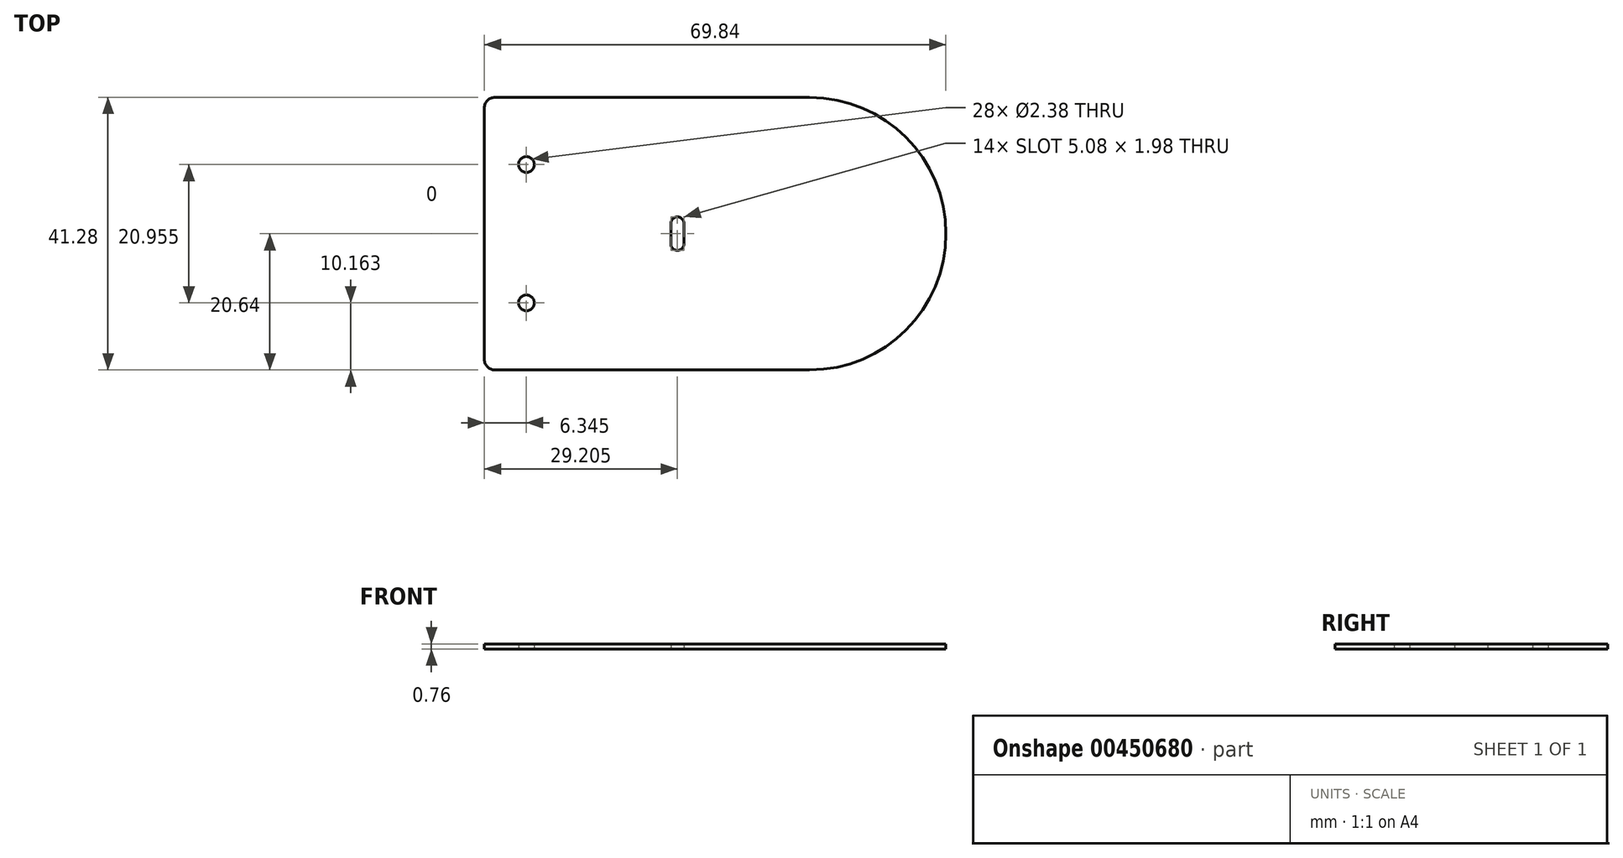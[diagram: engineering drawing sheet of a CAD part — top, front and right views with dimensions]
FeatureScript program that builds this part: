
annotation { "Feature Type Name" : "Feature", "Feature Type Description" : "" }
export const myFeature = defineFeature(function(context is Context, id is Id, definition is map)
    precondition{}
    {
        {
            var Q0;
            Q0=qCreatedBy(makeId("Top.planeOp"),FACE);
            var sketch = newSketch(context, id + "F0", { "sketchPlane" : qUnion([Q0])});
            skLineSegment(sketch, "E0.bottom", {"start": v(14.29, -20.64) * mm, "end": v(-33.34, -20.64) * mm});
            skLineSegment(sketch, "E0.top", {"start": v(14.29, 20.64) * mm, "end": v(-33.34, 20.64) * mm});
            skLineSegment(sketch, "E0.left", {"start": v(34.93, 0) * mm, "end": v(34.93, 0) * mm});
            skLineSegment(sketch, "E0.right", {"start": v(-34.93, -19.05) * mm, "end": v(-34.93, 19.05) * mm});
            skPoint(sketch, "E0.middle", {"position": v(0, 0) * mm});
            skPoint(sketch, "E1.visualSharp", {"position": v(34.93, 20.64) * mm});
            skArc(sketch, "E1.filletArc", {"start": v(34.93, 0) * mm, "mid": v(28.88, 14.6) * mm, "end": v(14.29, 20.64) * mm});
            skPoint(sketch, "E2.visualSharp", {"position": v(34.92, -20.64) * mm});
            skArc(sketch, "E2.filletArc", {"start": v(14.29, -20.64) * mm, "mid": v(28.88, -14.6) * mm, "end": v(34.92, 0) * mm});
            skPoint(sketch, "E3", {"position": v(-34.93, 0) * mm});
            skLineSegment(sketch, "E4.left", {"start": v(-4.72, -1.55) * mm, "end": v(-4.72, 1.55) * mm});
            skLineSegment(sketch, "E4.right", {"start": v(-6.7, -1.55) * mm, "end": v(-6.7, 1.55) * mm});
            skPoint(sketch, "E4.middle", {"position": v(-5.72, 0) * mm});
            skArc(sketch, "E5", {"start": v(-6.7, 1.55) * mm, "mid": v(-5.72, 2.54) * mm, "end": v(-4.72, 1.55) * mm});
            skArc(sketch, "E6", {"start": v(-6.7, -1.55) * mm, "mid": v(-5.72, -2.54) * mm, "end": v(-4.72, -1.55) * mm});
            skPoint(sketch, "E7", {"position": v(-5.72, 2.54) * mm});
            skPoint(sketch, "E8", {"position": v(-5.72, -2.54) * mm});
            skPoint(sketch, "E9.visualSharp", {"position": v(-34.93, 20.64) * mm});
            skArc(sketch, "E9.filletArc", {"start": v(-33.34, 20.64) * mm, "mid": v(-34.46, 20.17) * mm, "end": v(-34.93, 19.05) * mm});
            skPoint(sketch, "E10.visualSharp", {"position": v(-34.93, -20.64) * mm});
            skArc(sketch, "E10.filletArc", {"start": v(-34.92, -19.05) * mm, "mid": v(-34.46, -20.17) * mm, "end": v(-33.34, -20.64) * mm});
            skCircle(sketch, "E11", {"center": v(-28.58, 10.48) * mm, "radius": 1.2 * mm});
            skCircle(sketch, "E12.MirrorC", {"center": v(-28.58, -10.48) * mm, "radius": 1.2 * mm});
            skSolve(sketch);
        }
        {
            var Q0;
            Q0=makeQuery(id+"F0.imprint","IMPRINT",FACE,{"disambiguationData":[TD([[makeQuery(id+"F0.imprint","IMPRINT",EDGE,{"derivedFrom":sQuery(id+"F0.wireOp",EDGE,"E0.bottom")}),-1.0]])]});
            extrude(context, id + "F1", {"entities" : qUnion([Q0]), "depth" : 0.76 * mm});
        }
    });
